# Revit family: ASH_Contour21_S6472_BIM_GB
name_source: partatom
category: Plumbing Fixtures
revit_build: Autodesk Revit MEP 2014 (Build: 20130308_1515(x64)
units: mm (PartAtom-declared; Revit-internal decimal feet)

## types (4) — shared parameters
AccessibilityPerformance = Part-M
Accessories = www.idealspec.co.uk
AreaUnits = millimeters
Assembly Code = C1030200
AssetType = Fixed
Brand = Armitage Shanks
ConnectionType = Plumbing
Default Elevation = 680 mm  [stored 2.23097 ft]
Description = Contour 21 angled grab rail 45 x 45 x 35mm diameter
DurationUnit = year
ExpectedLife = 30
Features = Angled grab rail 45 x 45 x 35mm diameter
Finish = Chrome
Help = www.idealspec.co.uk/contact-us.html
IfcExportAs = IfcValveType
IfcExportType = FAUCET
InstallationInstructions = www.idealspec.co.uk/resources.html
LinearUnits = millimeters
ManufacturerURL = www.idealspec.co.uk
Material = Aluminium
ModelReference = Contour 21 angled grab rail 45 x 45 x 35mm diameter
NBSDescription = Support rails
NBSReference = 45-35-70/360
NettWeight = 1.53 Kg
Shape = Sculptured
Size = 0 x 0 x 0 mm
Space = Internal
SpareParts = www.fastpart-spares.co.uk
URL = www.idealspec.co.uk
Uniclass2015Code = Pr_40_20_76_84
Uniclass2015Title = Support rails
Uniclass2015Version = Products v1.1
Version = 1
VolumeUnits = Litres
WarrantyDescription = Manufacturers Warranty
WarrantyDurationParts = 5
WarrantyDurationUnit = year
zero-valued in all types: CWFU, Cost, HWFU, NominalHeight, NominalLength, NominalWidth, WFU

## per-type parameters (varying)
| type | BIMObjectName | BarCode | Color | GrabRailMtl | Model | ModelNumber | Name | ProductInformation |
| S647236 - Contour21 - Angled Grab Rail - 450 x 450mm - Blue | ASH_ArmitageShanks_SupportRails_Contour21_S647236 | 5017830385066 | Blue | ASH_ArmatigeShanks_Brassware_Blue_36_Render | S647236 | S647236 | SupportRails_Contour21_S647236_ArmitageShanks | www.idealspec.co.uk/assets/datasheet/S647236 |
| S6472AC - Contour21 - Angled Grab Rail - 450 x 450mm - White | ASH_ArmitageShanks_SupportRails_Contour21_S6472AC | 5017830383949 | White | ASH_ArmatigeShanks_Brassware_White_AC_Render | S6472AC | S6472AC | SupportRails_Contour21_S6472AC_ArmitageShanks | www.idealspec.co.uk/assets/datasheet/S6472AC |
| S6472LJ - Contour21 - Angled Grab Rail - 450 x 450mm - Light Grey | ASH_ArmitageShanks_SupportRails_Contour21_S6472LJ | 5017830384748 | Grey | ASH_ArmatigeShanks_Brassware_LightGrey_LJ_Render | S6472LJ | S6472LJ | SupportRails_Contour21_S6472LJ_ArmitageShanks | www.idealspec.co.uk/assets/datasheet/S6472LJ |
| S6472MY - Contour21 - Angled Grab Rail - 450 x 450mm - Stainless Steel | ASH_ArmitageShanks_SupportRails_Contour21_S6472MY | 5017830384427 | Stainless Steel finish | ASH_ArmatigeShanks_Brassware_Steel_MY_Render | S6472MY | S6472MY | SupportRails_Contour21_S6472MY_ArmitageShanks | www.idealspec.co.uk/assets/datasheet/S6472MY |

note: [stored X ft] marks values corroborated as IEEE doubles in the binary element streams (Revit-internal decimal feet)

## geometry (parser evidence)
native form markers: Sweep x6
no freeform markers — native parametric forms only
